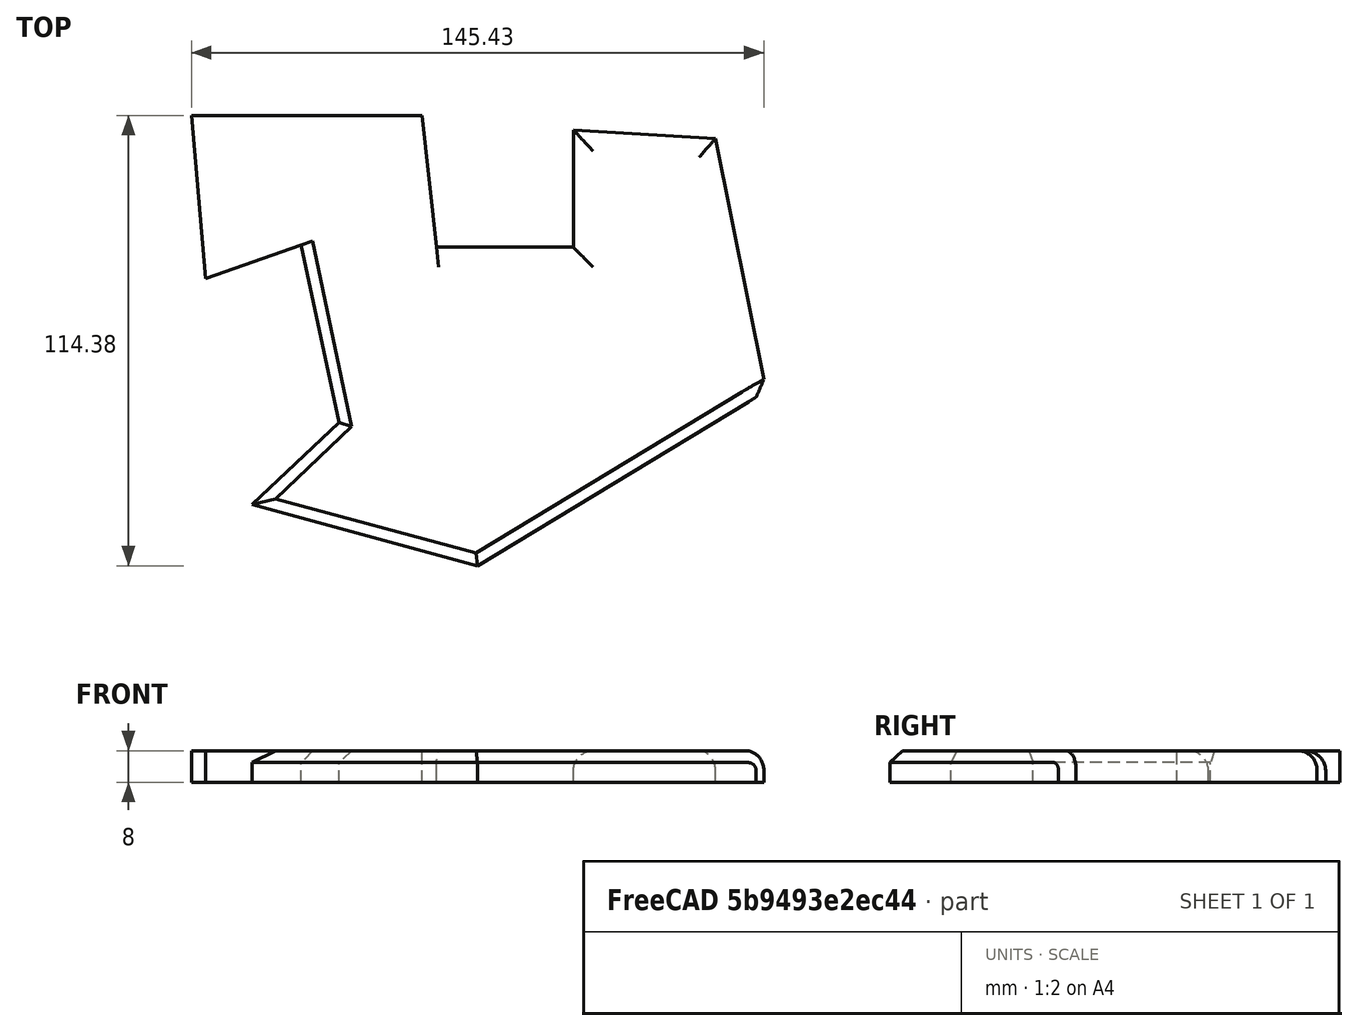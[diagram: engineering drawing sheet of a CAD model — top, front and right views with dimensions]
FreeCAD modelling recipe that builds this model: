
FCSTD DOCUMENT  (FreeCAD 0.18R13866 (Git))
Label: filletchamfer
License: All rights reserved
LicenseURL: http://en.wikipedia.org/wiki/All_rights_reserved
objects: Sketcher::SketchObject×1, PartDesign::Pad×1, PartDesign::Fillet×1, PartDesign::Chamfer×1, PartDesign::Body×1
note: 6 computed .brp shape members not serialized (recipe doc carries the construction recipe); baked Part::Feature solids carry a one-line shape summary decoded from their .brp

FEATURE [Sketcher::SketchObject] Sketch
  MapMode = 5
  Support = -> [XY_Plane]
  sketch-geometry (12):
    g0: LineSegment StartX=-46.7346 StartY=12.3768 StartZ=0 EndX=-22.4662 EndY=20.8739 EndZ=0
    g1: LineSegment StartX=-22.4662 StartY=20.8739 StartZ=0 EndX=-12.9199 EndY=-24.1962 EndZ=0
    g2: LineSegment StartX=-12.9199 StartY=-24.1962 StartZ=0 EndX=-34.8985 EndY=-45.0618 EndZ=0
    g3: LineSegment StartX=-34.8985 StartY=-45.0618 StartZ=0 EndX=22.379 EndY=-60.6022 EndZ=0
    g4: LineSegment StartX=22.379 StartY=-60.6022 StartZ=0 EndX=95.6409 EndY=-16.2011 EndZ=0
    g5: LineSegment StartX=95.6409 StartY=-16.2011 StartZ=0 EndX=82.7645 EndY=47.9586 EndZ=0
    g6: LineSegment StartX=82.7645 StartY=47.9586 StartZ=0 EndX=46.662 EndY=50.1329 EndZ=0
    g7: LineSegment StartX=46.662 StartY=50.1329 StartZ=0 EndX=46.662 EndY=20.3255 EndZ=0
    g8: LineSegment StartX=46.662 StartY=20.3255 StartZ=0 EndX=11.8867 EndY=20.3255 EndZ=0
    g9: LineSegment StartX=11.8867 StartY=20.3255 StartZ=0 EndX=8.24356 EndY=53.776 EndZ=0
    g10: LineSegment StartX=8.24356 StartY=53.776 StartZ=0 EndX=-50.3777 EndY=53.776 EndZ=0
    g11: LineSegment StartX=-50.3777 StartY=53.776 StartZ=0 EndX=-46.7346 EndY=12.3768 EndZ=0
  constraints (16):
    c: Coincident(g0,g1)
    c: Coincident(g1,g2)
    c: Coincident(g2,g3)
    c: Coincident(g3,g4)
    c: Coincident(g4,g5)
    c: Coincident(g5,g6)
    c: Coincident(g6,g7)
    c: Vertical(g7)
    c: Coincident(g7,g8)
    c: Horizontal(g8)
    c: Coincident(g8,g9)
    c: Coincident(g9,g10)
    c: Horizontal(g10)
    c: Coincident(g10,g11)
    c: Coincident(g11,g0)
    c: Distance(g1) = 46.07
FEATURE [PartDesign::Pad] Pad
  Length = 8
  Length2 = 100
  Profile = -> Sketch
  Type = 0
FEATURE [PartDesign::Fillet] Fillet
  Base = -> Pad [Edge28,Edge25,Edge22,Edge19]
  BaseFeature = -> Pad
  Radius = 5
FEATURE [PartDesign::Chamfer] Chamfer
  Base = -> Fillet [Edge4,Edge21,Edge23,Edge25]
  BaseFeature = -> Fillet
  Size = 3
FEATURE [PartDesign::Body] Body
  Group = -> [Sketch,Pad,Fillet,Chamfer]
  Origin = -> Origin
  Tip = -> Chamfer
